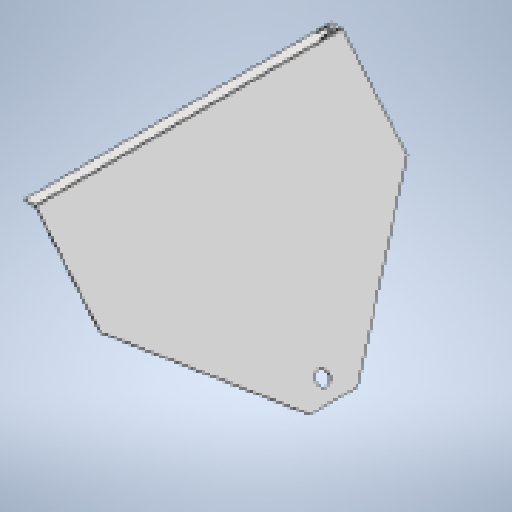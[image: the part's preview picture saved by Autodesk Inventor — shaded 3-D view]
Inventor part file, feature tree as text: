
AUTODESK INVENTOR PART (.ipt)
format: ipt  version: 2025 (Build 290162010, 162A)  size: 953,344 bytes
history: native  units: mm
features: sketch x4, other x4, sheet_metal_op x3, extrude x2
ambient origin geometry x8: Origin, YZ Plane, XZ Plane, XY Plane, X Axis, Y Axis, Z Axis, Center Point
bodies: Solid1 (feature_tree)
feature tree (13):
  sheet_metal_op  "Contour Flange1"
  sketch  "Sketch18"  dims[d10=4.0mm]
  extrude  "Extrusion9"  Depth=4.0mm
  other  "A-Side Definition"
  other  "Mark1"
  extrude  "Extrusion10"  Depth=8.0mm
  sketch  "Sketch1"  dims[d6=4.0mm d7=4.0mm]
  other  "Plate1"
  sheet_metal_op  "Bend1"
  sheet_metal_op  "Corner1"
  sketch  "Sketch16"  dims[d8=2.0mm d9=8.0mm]
  sketch  "Sketch19"  dims[d11=1700.0mm d12=4.0mm d13=4.0mm d14=16.0mm d15=4.0mm d16=4.0mm d66=1150.0mm d68=60.0mm d69=845.0mm d70=8.0mm d80=8.726646mm d108=264.41mm d109=675.443mm d110=693.166574mm d111=10.0mm d112=0.0mm d123=76.5mm d124=100.0mm d125=0.0mm d126=0.0mm d127=30.0mm d128=23.736478mm]
  other  "Definition1"
